# Revit family: Door-Sectional_Model2731_Comcl_Amarr
name_source: partatom
category: Doors
units: mm (PartAtom-declared; Revit-internal decimal feet)

## family parameters
Always vertical = Yes
Classification Number = 23.30.10.17.37.14
Cut with Voids When Loaded = No
Host = Wall
Room Calculation Point = No
Shared = No

## types (1)
- ByType
    21" Section Heights = Yes
    24" Section Heights = No
    2nd Row Elevation = 1' - 9"
    3nd Row Elevation = 3' - 6"
    3rd Row Section Type = Section-Backer : ByType
    4th Row Elevation = 5' - 3"
    5th Row Elevation = 7' - 0"
    Analytic Construction = <None>
    Assembly Code = B2030410
    Construction Details = https://www.arcat.com
    Cost = 0 $
    Description = Door Sectional Model 2731 Commercial
    Door Cladding Material = Steel - 27 GA Exterior_27 GA Interior
    Door Gap From Wall Interior = 0' - 0 11/32"
    Door Glazing = Plexiglas
    Door Open = Yes
    Door Track Material = Steel - 19 GA galvanized
    Fire Rating = As Specified in 08 36 00
    Function = Interior
    Green Building-LEED = https://www.arcat.com
    Has 4 Sections = No
    Has Greater Than 4 Sections = Yes
    Has Operator = Yes
    Height = 8' - 0"
    Keynote = 08 36 00
    Manufacturer = Amarr Garage Doors
    Model = 2731
    Number of Horizontal Windows = 2
    Number of Panels Above 3rd = 2
    Number of Sections = 5
    Operator Material = Metal - Aluminum
    Panel Width = 10' - 2"
    Product Data = http://www.arcat.com
    Rough Height = 0' - 0"
    Rough Width = 0' - 0"
    Section Heights = 1' - 9"
    Section Heights XX = 2' - 0"
    Specification = https://www.arcat.com
    Stile Material = Metal - Aluminum
    Thickness = 0' - 2"
    Track Width = 10' - 3 9/16"
    URL = https://www.amarr.com
    Wall Closure = By host
    Width = 10' - 0"
    eb End Stiles = 0' - 3 3/8"
    eb Intermediate Rails = 0' - 1 1/4"
    eb Middle Stile Width = 0' - 2 1/2"
    eb Number of Extra Sections = 0
    eb Operator Centerline Offset from Panel Face = 0' - 3 1/32"
    eb Shaft Centerline from TO Door = 1' - 0 1/2"
    eb Track Thickness = 0' - 2"

## geometry (parser evidence)
native form markers: Sweep x29
no freeform markers — native parametric forms only
